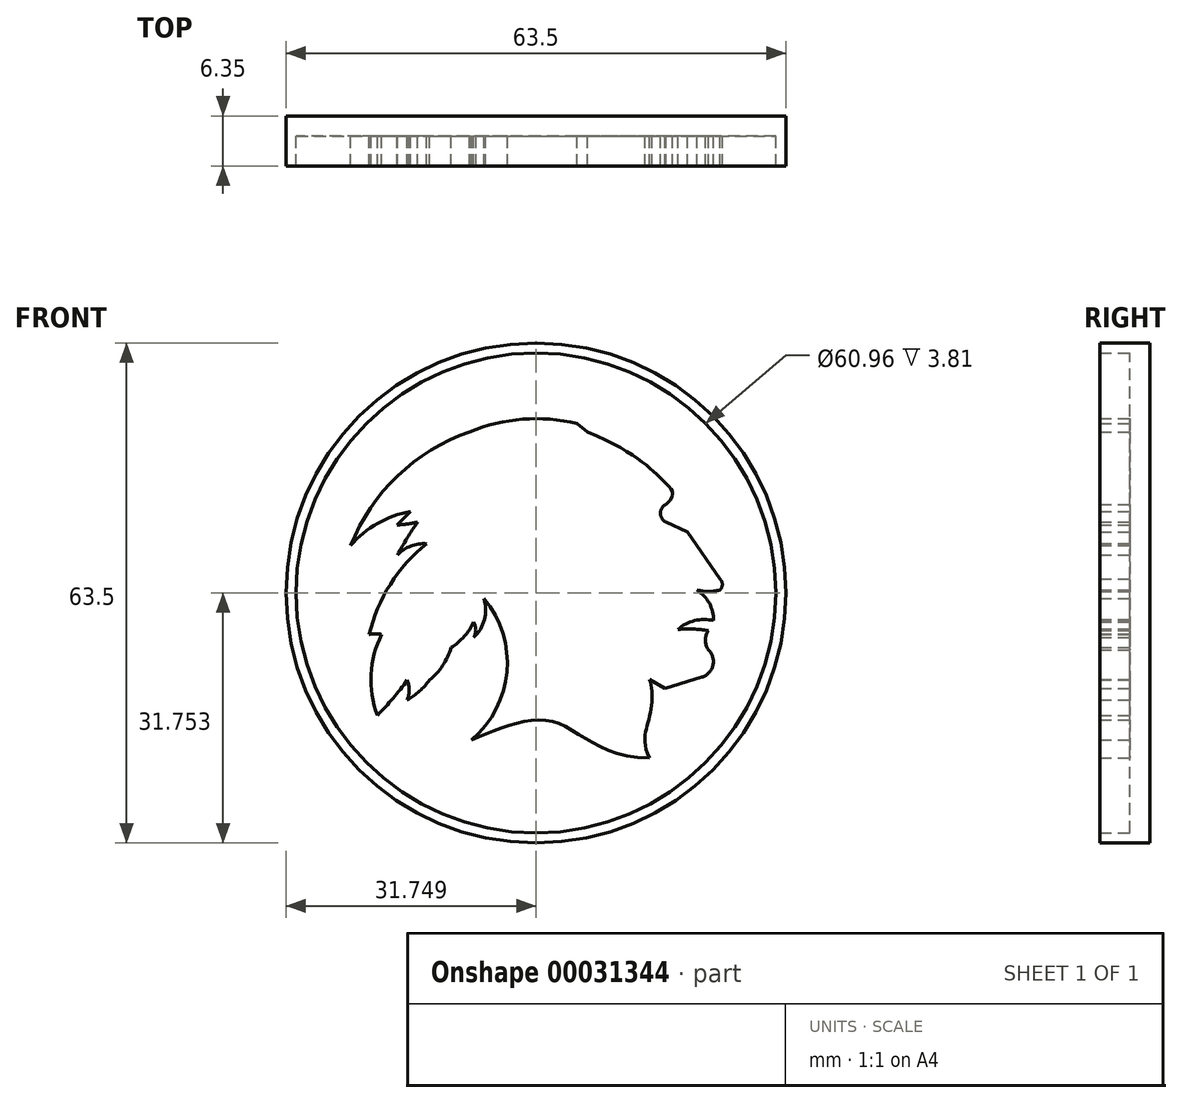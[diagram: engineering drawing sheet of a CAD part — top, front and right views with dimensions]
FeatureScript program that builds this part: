
annotation { "Feature Type Name" : "Feature", "Feature Type Description" : "" }
export const myFeature = defineFeature(function(context is Context, id is Id, definition is map)
    precondition{}
    {
        {
            var Q0;
            Q0=qCreatedBy(makeId("Front.planeOp"),FACE);
            var sketch = newSketch(context, id + "F0", { "sketchPlane" : qUnion([Q0])});
            skFitSpline(sketch, "E0", {"points": [v(-11.98, -18.12) * mm, v(-1.87, -15.72) * mm, v(10.63, -20.38) * mm], "startDerivative": vector(21.1, 8.36) * mm, "endDerivative": vector(36.05, 0.75) * mm});
            skFitSpline(sketch, "E1", {"points": [v(10.63, -20.38) * mm, v(10.63, -15.2) * mm, v(10.63, -10.4) * mm], "startDerivative": vector(-6.26, 13.3) * mm, "endDerivative": vector(-3.26, 7.33) * mm});
            skLineSegment(sketch, "E2", {"start": v(10.63, -10.4) * mm, "end": v(12.61, -11.6) * mm});
            skLineSegment(sketch, "E3", {"start": v(12.61, -11.6) * mm, "end": v(17.3, -10.13) * mm});
            skArc(sketch, "E4", {"start": v(17.3, -10.13) * mm, "mid": v(18.7, -8.63) * mm, "end": v(18.13, -6.65) * mm});
            skArc(sketch, "E5", {"start": v(18.13, -4.23) * mm, "mid": v(17.76, -5.44) * mm, "end": v(18.13, -6.65) * mm});
            skArc(sketch, "E6", {"start": v(18.13, -4.23) * mm, "mid": v(16.2, -4.03) * mm, "end": v(14.25, -4.07) * mm});
            skArc(sketch, "E7", {"start": v(18.78, -2.96) * mm, "mid": v(18.24, -0.75) * mm, "end": v(16.68, 0.92) * mm});
            skPoint(sketch, "E7.startSnap0", {"position": v(16.42, -2.96) * mm});
            skPoint(sketch, "E8.orphan", {"position": v(18.78, -4.07) * mm});
            skArc(sketch, "E9", {"start": v(18.78, -2.96) * mm, "mid": v(16.38, -2.97) * mm, "end": v(14.25, -4.07) * mm});
            skArc(sketch, "E10", {"start": v(16.68, 0.92) * mm, "mid": v(18.13, 0.75) * mm, "end": v(19.57, 0.92) * mm});
            skArc(sketch, "E11", {"start": v(19.57, 0.92) * mm, "mid": v(19.9, 1.64) * mm, "end": v(19.57, 2.36) * mm});
            skLineSegment(sketch, "E12", {"start": v(19.57, 2.36) * mm, "end": v(15.5, 8.28) * mm});
            skLineSegment(sketch, "E13", {"start": v(15.5, 8.28) * mm, "end": v(12.74, 9.57) * mm});
            skArc(sketch, "E14", {"start": v(12.74, 11.8) * mm, "mid": v(12.03, 10.69) * mm, "end": v(12.74, 9.57) * mm});
            skFitSpline(sketch, "E15", {"points": [v(12.74, 11.8) * mm, v(12.74, 14.45) * mm, v(2.76, 21.02) * mm], "startDerivative": vector(13.55, 12.48) * mm, "endDerivative": vector(-28.97, 12.17) * mm});
            skLineSegment(sketch, "E16", {"start": v(2.76, 21.02) * mm, "end": v(1.44, 22.07) * mm});
            skArc(sketch, "E17", {"start": v(1.44, 22.07) * mm, "mid": v(-5.47, 22.63) * mm, "end": v(-12.22, 21.02) * mm});
            skArc(sketch, "E18", {"start": v(-12.22, 21.02) * mm, "mid": v(-21.34, 15.43) * mm, "end": v(-27.32, 6.57) * mm});
            skArc(sketch, "E19", {"start": v(-17.67, -5.07) * mm, "mid": v(-17.35, -3.17) * mm, "end": v(-17.67, -1.27) * mm});
            skArc(sketch, "E20", {"start": v(-17.28, -10.52) * mm, "mid": v(-15.62, -8.65) * mm, "end": v(-14.55, -6.4) * mm});
            skArc(sketch, "E21", {"start": v(-20.12, -13.04) * mm, "mid": v(-18.58, -11.92) * mm, "end": v(-17.28, -10.52) * mm});
            skArc(sketch, "E22", {"start": v(-20.12, -13.04) * mm, "mid": v(-19.9, -11.78) * mm, "end": v(-20.12, -10.52) * mm});
            skArc(sketch, "E23", {"start": v(-23.9, -14.97) * mm, "mid": v(-21.93, -12.82) * mm, "end": v(-20.12, -10.52) * mm});
            skArc(sketch, "E24", {"start": v(-23.38, -4.73) * mm, "mid": v(-24.72, -9.8) * mm, "end": v(-23.9, -14.97) * mm});
            skArc(sketch, "E25", {"start": v(-23.38, -4.73) * mm, "mid": v(-24.17, -4.63) * mm, "end": v(-24.96, -4.73) * mm});
            skArc(sketch, "E26", {"start": v(-17.67, 6.8) * mm, "mid": v(-22.28, 1.65) * mm, "end": v(-24.96, -4.73) * mm});
            skLineSegment(sketch, "E27", {"start": v(-17.67, 6.8) * mm, "end": v(-17.67, 6.8) * mm});
            skArc(sketch, "E28", {"start": v(-19.7, 10.9) * mm, "mid": v(-23.88, 9.39) * mm, "end": v(-27.32, 6.57) * mm});
            skLineSegment(sketch, "E29", {"start": v(-19.7, 10.9) * mm, "end": v(-21.41, 9.2) * mm});
            skArc(sketch, "E30", {"start": v(-21.41, 9.2) * mm, "mid": v(-15.49, 10.66) * mm, "end": v(-10.5, 14.19) * mm});
            skArc(sketch, "E31", {"start": v(-10.5, 14.19) * mm, "mid": v(-7.6, 16.74) * mm, "end": v(-5.91, 20.23) * mm});
            skArc(sketch, "E32", {"start": v(-11.98, -18.12) * mm, "mid": v(-7.47, -9.45) * mm, "end": v(-10.38, -0.13) * mm});
            skArc(sketch, "E33", {"start": v(-11.7, -5.12) * mm, "mid": v(-10.32, -2.81) * mm, "end": v(-10.38, -0.13) * mm});
            skArc(sketch, "E34", {"start": v(-11.7, -5.12) * mm, "mid": v(-11.42, -4.14) * mm, "end": v(-11.7, -3.15) * mm});
            skArc(sketch, "E35", {"start": v(-14.55, -6.4) * mm, "mid": v(-12.88, -4.98) * mm, "end": v(-11.7, -3.15) * mm});
            skArc(sketch, "E36", {"start": v(-17.67, 6.8) * mm, "mid": v(-19.66, 6.51) * mm, "end": v(-21.34, 5.39) * mm});
            skPoint(sketch, "E36.endSnap0", {"position": v(-21.34, 15.43) * mm});
            skArc(sketch, "E37", {"start": v(-18.8, 9.55) * mm, "mid": v(-20.15, 7.52) * mm, "end": v(-21.34, 5.39) * mm});
            skLineSegment(sketch, "E38", {"start": v(-9.5, -1.33) * mm, "end": v(-6.7, 2.36) * mm});
            skArc(sketch, "E39", {"start": v(-8.8, 7.62) * mm, "mid": v(-8.3, 4.77) * mm, "end": v(-6.7, 2.36) * mm});
            skArc(sketch, "E40", {"start": v(-8.8, 7.62) * mm, "mid": v(-7.4, 5.83) * mm, "end": v(-5.39, 4.77) * mm});
            skPoint(sketch, "E40.endSnap0", {"position": v(-8.3, 4.77) * mm});
            skArc(sketch, "E41", {"start": v(-3.94, 7.36) * mm, "mid": v(-5.21, 6.37) * mm, "end": v(-5.39, 4.77) * mm});
            skArc(sketch, "E42", {"start": v(-5.91, 10.77) * mm, "mid": v(-5.22, 8.9) * mm, "end": v(-3.94, 7.36) * mm});
            skArc(sketch, "E43", {"start": v(-5.91, 10.77) * mm, "mid": v(-4.62, 9.35) * mm, "end": v(-2.76, 8.93) * mm});
            skLineSegment(sketch, "E44", {"start": v(-2.76, 8.93) * mm, "end": v(-3.02, 12.1) * mm});
            skArc(sketch, "E45", {"start": v(-5.91, 20.23) * mm, "mid": v(-5.25, 15.89) * mm, "end": v(-3.02, 12.1) * mm});
            skArc(sketch, "E46", {"start": v(-5.91, 20.23) * mm, "mid": v(-9, 21.1) * mm, "end": v(-12.22, 21.02) * mm});
            skSolve(sketch);
        }
        {
            var Q0;
            {var subQ2=sQuery(id+"F0.wireOp",EDGE,"E0");Q0=makeQuery(id+"F0.imprint","IMPRINT",FACE,{"disambiguationData":[TD([[makeQuery(id+"F0.imprint","IMPRINT",EDGE,{"derivedFrom":subQ2}),1.0]])]});}
            var Q1;
            Q1=makeQuery(id+"F0.imprint","IMPRINT",FACE,{"disambiguationData":[TD([[makeQuery(id+"F0.imprint","IMPRINT",EDGE,{"derivedFrom":sQuery(id+"F0.wireOp",EDGE,"E20")}),1.0]])]});
            var Q2;
            Q2=makeQuery(id+"F0.imprint","IMPRINT",FACE,{"disambiguationData":[TD([[makeQuery(id+"F0.imprint","IMPRINT",EDGE,{"derivedFrom":sQuery(id+"F0.wireOp",EDGE,"E18")}),1.0]])]});
            extrude(context, id + "F1", {"entities" : qUnion([Q0, Q1, Q2]), "depth" : 3.8 * mm});
        }
        {
            var Q0;
            Q0=makeQuery(id+"F1.opExtrude","CAP_FACE",FACE,{"disambiguationData":[OSD([sQuery(id+"F0.wireOp",EDGE,"E0"),sQuery(id+"F0.wireOp",EDGE,"E1"),sQuery(id+"F0.wireOp",EDGE,"E2"),sQuery(id+"F0.wireOp",EDGE,"E3"),sQuery(id+"F0.wireOp",EDGE,"E4"),sQuery(id+"F0.wireOp",EDGE,"E5"),sQuery(id+"F0.wireOp",EDGE,"E6"),sQuery(id+"F0.wireOp",EDGE,"E7"),sQuery(id+"F0.wireOp",EDGE,"E9"),sQuery(id+"F0.wireOp",EDGE,"E10"),sQuery(id+"F0.wireOp",EDGE,"E11"),sQuery(id+"F0.wireOp",EDGE,"E12"),sQuery(id+"F0.wireOp",EDGE,"E13"),sQuery(id+"F0.wireOp",EDGE,"E14"),sQuery(id+"F0.wireOp",EDGE,"E15"),sQuery(id+"F0.wireOp",EDGE,"E16"),sQuery(id+"F0.wireOp",EDGE,"E17"),sQuery(id+"F0.wireOp",EDGE,"E18"),sQuery(id+"F0.wireOp",EDGE,"E20"),sQuery(id+"F0.wireOp",EDGE,"E21"),sQuery(id+"F0.wireOp",EDGE,"E22"),sQuery(id+"F0.wireOp",EDGE,"E23"),sQuery(id+"F0.wireOp",EDGE,"E24"),sQuery(id+"F0.wireOp",EDGE,"E25"),sQuery(id+"F0.wireOp",EDGE,"E26"),sQuery(id+"F0.wireOp",EDGE,"E28"),sQuery(id+"F0.wireOp",EDGE,"E29"),sQuery(id+"F0.wireOp",EDGE,"E30"),sQuery(id+"F0.wireOp",EDGE,"E32"),sQuery(id+"F0.wireOp",EDGE,"E33"),sQuery(id+"F0.wireOp",EDGE,"E34"),sQuery(id+"F0.wireOp",EDGE,"E35"),sQuery(id+"F0.wireOp",EDGE,"E36"),sQuery(id+"F0.wireOp",EDGE,"E37")])],"isStart":true});
            var sketch = newSketch(context, id + "F2", { "sketchPlane" : qUnion([Q0])});
            skCircle(sketch, "E47", {"center": v(3.77, 0.55) * mm, "radius": 31.75 * mm});
            skSolve(sketch);
        }
        {
            var Q0;
            Q0=makeQuery(id+"F2.imprint","IMPRINT",FACE,{"disambiguationData":[TD([[makeQuery(id+"F2.imprint","IMPRINT",EDGE,{"derivedFrom":sQuery(id+"F2.wireOp",EDGE,"E47")}),1.0]])]});
            var Q1;
            Q1=makeQuery(id+"F2.imprint","IMPRINT",FACE,{"disambiguationData":[TD([[makeQuery(id+"F2.imprint","IMPRINT",EDGE,{"derivedFrom":makeQuery(id+"F1.opExtrude","CAP_EDGE",EDGE,{"disambiguationData":[OSD([sQuery(id+"F0.wireOp",EDGE,"E0")])],"isStart":true})}),-1.0]])]});
            extrude(context, id + "F3", {"entities" : qUnion([Q0, Q1]), "depth" : 2.54 * mm});
        }
        {
            var Q0;
            Q0=makeQuery(id+"F3.opExtrude","CAP_FACE",FACE,{"disambiguationData":[OSD([sQuery(id+"F0.wireOp",EDGE,"E0"),sQuery(id+"F0.wireOp",EDGE,"E1"),sQuery(id+"F0.wireOp",EDGE,"E2"),sQuery(id+"F0.wireOp",EDGE,"E3"),sQuery(id+"F0.wireOp",EDGE,"E4"),sQuery(id+"F0.wireOp",EDGE,"E5"),sQuery(id+"F0.wireOp",EDGE,"E6"),sQuery(id+"F0.wireOp",EDGE,"E7"),sQuery(id+"F0.wireOp",EDGE,"E9"),sQuery(id+"F0.wireOp",EDGE,"E10"),sQuery(id+"F0.wireOp",EDGE,"E11"),sQuery(id+"F0.wireOp",EDGE,"E12"),sQuery(id+"F0.wireOp",EDGE,"E13"),sQuery(id+"F0.wireOp",EDGE,"E14"),sQuery(id+"F0.wireOp",EDGE,"E15"),sQuery(id+"F0.wireOp",EDGE,"E16"),sQuery(id+"F0.wireOp",EDGE,"E17"),sQuery(id+"F0.wireOp",EDGE,"E18"),sQuery(id+"F0.wireOp",EDGE,"E20"),sQuery(id+"F0.wireOp",EDGE,"E21"),sQuery(id+"F0.wireOp",EDGE,"E22"),sQuery(id+"F0.wireOp",EDGE,"E23"),sQuery(id+"F0.wireOp",EDGE,"E24"),sQuery(id+"F0.wireOp",EDGE,"E25"),sQuery(id+"F0.wireOp",EDGE,"E26"),sQuery(id+"F0.wireOp",EDGE,"E28"),sQuery(id+"F0.wireOp",EDGE,"E29"),sQuery(id+"F0.wireOp",EDGE,"E30"),sQuery(id+"F0.wireOp",EDGE,"E32"),sQuery(id+"F0.wireOp",EDGE,"E33"),sQuery(id+"F0.wireOp",EDGE,"E34"),sQuery(id+"F0.wireOp",EDGE,"E35"),sQuery(id+"F0.wireOp",EDGE,"E36"),sQuery(id+"F0.wireOp",EDGE,"E37"),sQuery(id+"F2.wireOp",EDGE,"E47")])],"isStart":true});
            var sketch = newSketch(context, id + "F4", { "sketchPlane" : qUnion([Q0])});
            skCircle(sketch, "E48.0", {"center": v(-3.77, 0.55) * mm, "radius": 31.75 * mm});
            skCircle(sketch, "E49.0", {"center": v(-3.77, 0.55) * mm, "radius": 30.48 * mm});
            skSolve(sketch);
        }
        {
            var Q0;
            Q0=makeQuery(id+"F4.imprint","IMPRINT",FACE,{"disambiguationData":[TD([[makeQuery(id+"F4.imprint","IMPRINT",EDGE,{"derivedFrom":sQuery(id+"F4.wireOp",EDGE,"E48.0")}),-1.0]])]});
            extrude(context, id + "F5", {"entities" : qUnion([Q0]), "operationType" : NewBodyOperationType.ADD, "depth" : 3.8 * mm});
        }
    });
